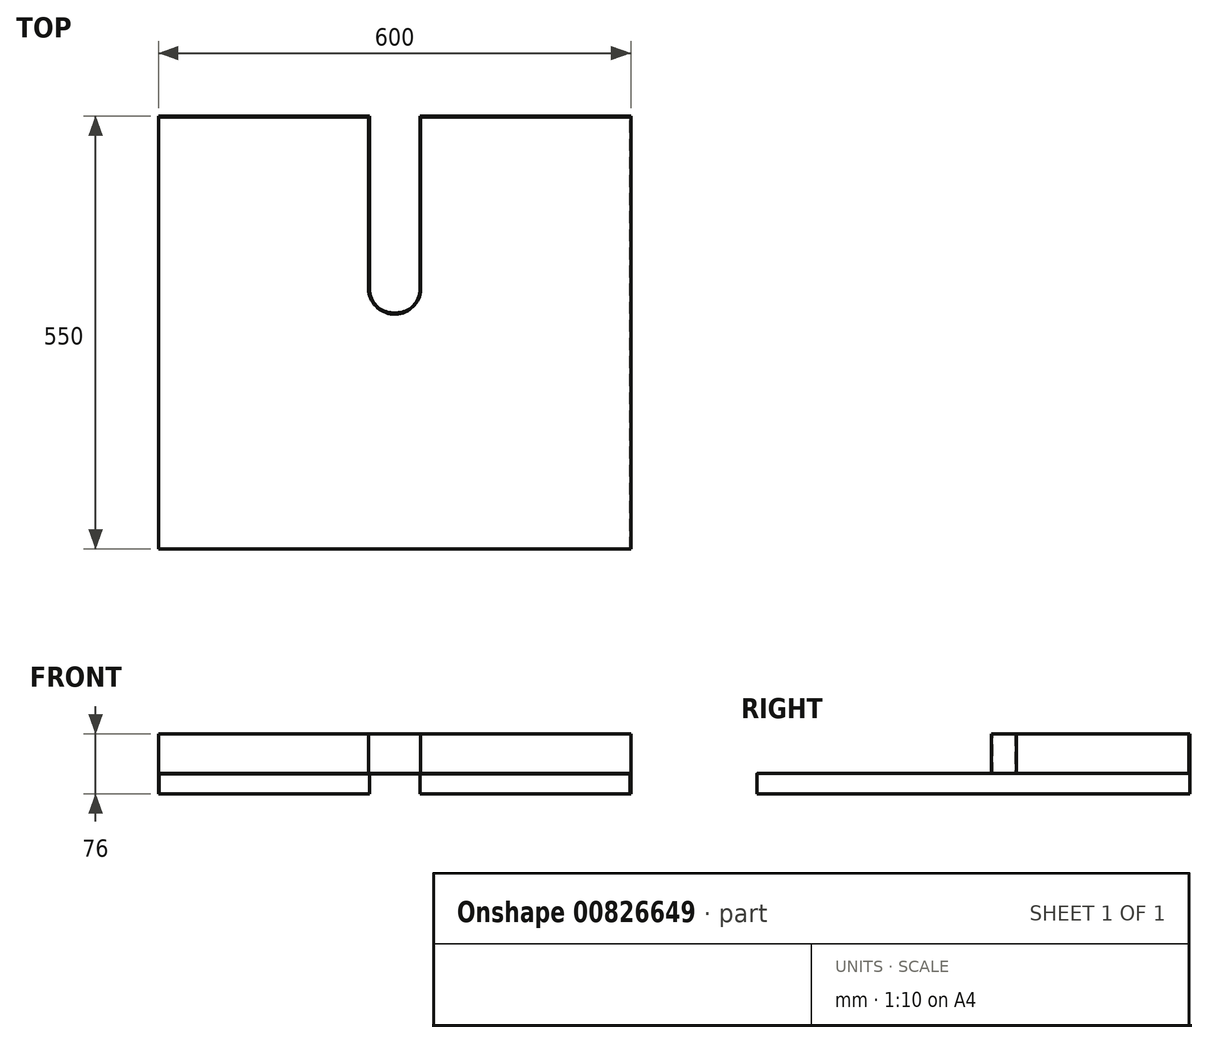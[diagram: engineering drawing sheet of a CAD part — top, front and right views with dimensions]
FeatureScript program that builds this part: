
annotation { "Feature Type Name" : "Feature", "Feature Type Description" : "" }
export const myFeature = defineFeature(function(context is Context, id is Id, definition is map)
    precondition{}
    {
        {
            var Q0;
            Q0=qCreatedBy(makeId("Top.planeOp"),FACE);
            var sketch = newSketch(context, id + "F0", { "sketchPlane" : qUnion([Q0])});
            skLineSegment(sketch, "E0.bottom", {"start": v(300, -275) * mm, "end": v(-300, -275) * mm});
            skLineSegment(sketch, "E0.top", {"start": v(300, 275) * mm, "end": v(-300, 275) * mm});
            skLineSegment(sketch, "E0.left", {"start": v(300, -275) * mm, "end": v(300, 275) * mm});
            skLineSegment(sketch, "E0.right", {"start": v(-300, -275) * mm, "end": v(-300, 275) * mm});
            skPoint(sketch, "E0.middle", {"position": v(0, 0) * mm});
            skSolve(sketch);
        }
        {
            var Q0;
            Q0=makeQuery(id+"F0.imprint","IMPRINT",FACE,{"disambiguationData":[TD([[makeQuery(id+"F0.imprint","IMPRINT",EDGE,{"derivedFrom":sQuery(id+"F0.wireOp",EDGE,"E0.bottom")}),-1.0]])]});
            extrude(context, id + "F1", {"entities" : qUnion([Q0]), "depth" : 1 * mm, "offsetDistance" : 25 * mm});
        }
        {
            var Q0;
            Q0=makeQuery(id+"F1.opExtrude","CAP_FACE",FACE,{"disambiguationData":[OSD([sQuery(id+"F0.wireOp",EDGE,"E0.bottom"),sQuery(id+"F0.wireOp",EDGE,"E0.top"),sQuery(id+"F0.wireOp",EDGE,"E0.left"),sQuery(id+"F0.wireOp",EDGE,"E0.right")])],"isStart":true});
            var sketch = newSketch(context, id + "F2", { "sketchPlane" : qUnion([Q0])});
            skLineSegment(sketch, "E1", {"start": v(299, 275) * mm, "end": v(299, -274) * mm});
            skLineSegment(sketch, "E2", {"start": v(-299, 275) * mm, "end": v(-299, -274) * mm});
            skLineSegment(sketch, "E3", {"start": v(-299, -274) * mm, "end": v(299, -274) * mm});
            skSolve(sketch);
        }
        {
            var Q0;
            {var subQ1=sQuery(id+"F2.wireOp",EDGE,"E1");Q0=makeQuery(id+"F2.imprint","IMPRINT",FACE,{"disambiguationData":[TD([[makeQuery(id+"F2.imprint","IMPRINT",EDGE,{"derivedFrom":subQ1}),1.0]])]});}
            extrude(context, id + "F3", {"entities" : qUnion([Q0]), "operationType" : NewBodyOperationType.ADD, "depth" : 25 * mm, "offsetDistance" : 25 * mm});
        }
        {
            var Q0;
            Q0=makeQuery(id+"F1.opExtrude","CAP_FACE",FACE,{"disambiguationData":[OSD([sQuery(id+"F0.wireOp",EDGE,"E0.bottom"),sQuery(id+"F0.wireOp",EDGE,"E0.top"),sQuery(id+"F0.wireOp",EDGE,"E0.left"),sQuery(id+"F0.wireOp",EDGE,"E0.right")])],"isStart":false});
            var sketch = newSketch(context, id + "F4", { "sketchPlane" : qUnion([Q0])});
            skLineSegment(sketch, "E4", {"start": v(0, 275) * mm, "end": v(0, -275) * mm, "construction": true});
            skLineSegment(sketch, "E5.bottom", {"start": v(32.08, 275) * mm, "end": v(-32.08, 275) * mm});
            skLineSegment(sketch, "E5.top", {"start": v(2.08, 25) * mm, "end": v(-2.08, 25) * mm});
            skLineSegment(sketch, "E5.left", {"start": v(32.08, 275) * mm, "end": v(32.08, 55) * mm});
            skLineSegment(sketch, "E5.right", {"start": v(-32.08, 275) * mm, "end": v(-32.08, 55) * mm});
            skPoint(sketch, "E5.middle", {"position": v(0, 150) * mm});
            skPoint(sketch, "E6.visualSharp", {"position": v(32.08, 25) * mm});
            skArc(sketch, "E6.filletArc", {"start": v(2.08, 25) * mm, "mid": v(23.3, 33.79) * mm, "end": v(32.08, 55) * mm});
            skPoint(sketch, "E7.visualSharp", {"position": v(-32.08, 25) * mm});
            skArc(sketch, "E7.filletArc", {"start": v(-32.08, 55) * mm, "mid": v(-23.3, 33.79) * mm, "end": v(-2.08, 25) * mm});
            skArc(sketch, "E8.0", {"start": v(-37.08, 55) * mm, "mid": v(-26.83, 30.25) * mm, "end": v(-2.08, 20) * mm});
            skLineSegment(sketch, "E8.1", {"start": v(-37.08, 275) * mm, "end": v(-37.08, 55) * mm});
            skLineSegment(sketch, "E9.MirrorCS", {"start": v(37.08, 275) * mm, "end": v(37.08, 55) * mm});
            skArc(sketch, "E10.MirrorCS", {"start": v(37.08, 55) * mm, "mid": v(26.83, 30.25) * mm, "end": v(2.08, 20) * mm});
            skSolve(sketch);
        }
        {
            var Q0;
            Q0=makeQuery(id+"F4.imprint","IMPRINT",FACE,{"disambiguationData":[TD([[makeQuery(id+"F4.imprint","IMPRINT",EDGE,{"derivedFrom":sQuery(id+"F4.wireOp",EDGE,"E5.bottom")}),1.0]])]});
            extrude(context, id + "F5", {"entities" : qUnion([Q0]), "operationType" : NewBodyOperationType.REMOVE, "endBound" : BoundingType.THROUGH_ALL, "oppositeDirection" : true, "depth" : 25 * mm, "offsetDistance" : 25 * mm});
        }
        {
            var Q0;
            Q0=makeQuery(id+"F1.opExtrude","CAP_FACE",FACE,{"disambiguationData":[OSD([sQuery(id+"F0.wireOp",EDGE,"E0.bottom"),sQuery(id+"F0.wireOp",EDGE,"E0.top"),sQuery(id+"F0.wireOp",EDGE,"E0.left"),sQuery(id+"F0.wireOp",EDGE,"E0.right")])],"isStart":false});
            var sketch = newSketch(context, id + "F6", { "sketchPlane" : qUnion([Q0])});
            skLineSegment(sketch, "E11", {"start": v(-33.08, 275) * mm, "end": v(-33.08, 52.7) * mm});
            skLineSegment(sketch, "E12", {"start": v(33.08, 275) * mm, "end": v(33.08, 55) * mm});
            skPoint(sketch, "E13.1.internal.snap0", {"position": v(0, 25) * mm});
            skArc(sketch, "E14", {"start": v(-33.08, 52.7) * mm, "mid": v(1.07, 23.3) * mm, "end": v(33.08, 55) * mm});
            skSolve(sketch);
        }
        {
            var Q0;
            Q0 = qSketchRegion(id + "F6", true);
            var Q1;
            {var subQ11=sQuery(id+"F6.wireOp",EDGE,"E11");Q1=makeQuery(id+"F6.imprint","IMPRINT",FACE,{"disambiguationData":[TD([[makeQuery(id+"F6.imprint","IMPRINT",EDGE,{"derivedFrom":subQ11}),1.0]])]});}
            extrude(context, id + "F7", {"entities" : qUnion([Q0, Q1]), "operationType" : NewBodyOperationType.ADD, "depth" : 50 * mm, "offsetDistance" : 25 * mm});
        }
        {
            var Q0;
            Q0=makeQuery(id+"F1.opExtrude","CAP_FACE",FACE,{"disambiguationData":[OSD([sQuery(id+"F0.wireOp",EDGE,"E0.bottom"),sQuery(id+"F0.wireOp",EDGE,"E0.top"),sQuery(id+"F0.wireOp",EDGE,"E0.left"),sQuery(id+"F0.wireOp",EDGE,"E0.right")])],"isStart":false});
            var sketch = newSketch(context, id + "F8", { "sketchPlane" : qUnion([Q0])});
            skLineSegment(sketch, "E15", {"start": v(-300, 274) * mm, "end": v(-33.08, 274) * mm});
            skLineSegment(sketch, "E16", {"start": v(33.08, 274) * mm, "end": v(300, 274) * mm});
            skSolve(sketch);
        }
        {
            var Q0;
            Q0 = qSketchRegion(id + "F8", true);
            var Q1;
            {var subQ0=sQuery(id+"F8.wireOp",EDGE,"E15");Q1=makeQuery(id+"F8.imprint","IMPRINT",FACE,{"disambiguationData":[TD([[makeQuery(id+"F8.imprint","IMPRINT",EDGE,{"derivedFrom":subQ0}),1.0]])]});}
            var Q2;
            {var subQ0=sQuery(id+"F8.wireOp",EDGE,"E16");Q2=makeQuery(id+"F8.imprint","IMPRINT",FACE,{"disambiguationData":[TD([[makeQuery(id+"F8.imprint","IMPRINT",EDGE,{"derivedFrom":subQ0}),1.0]])]});}
            extrude(context, id + "F9", {"entities" : qUnion([Q0, Q1, Q2]), "operationType" : NewBodyOperationType.ADD, "depth" : 50 * mm, "offsetDistance" : 25 * mm});
        }
        {
            var Q0;
            Q0=makeQuery(id+"F1.opExtrude","CAP_EDGE",EDGE,{"disambiguationData":[OSD([sQuery(id+"F0.wireOp",EDGE,"E0.right")])],"isStart":false});
            var Q1;
            Q1=makeQuery(id+"F1.opExtrude","CAP_EDGE",EDGE,{"disambiguationData":[OSD([sQuery(id+"F0.wireOp",EDGE,"E0.bottom")])],"isStart":false});
            var Q2;
            Q2=makeQuery(id+"F1.opExtrude","CAP_EDGE",EDGE,{"disambiguationData":[OSD([sQuery(id+"F0.wireOp",EDGE,"E0.left")])],"isStart":false});
            var Q3;
            Q3=makeQuery(id+"F9.opExtrude","CAP_EDGE",EDGE,{"disambiguationData":[OSD([sQuery(id+"F8.wireOp",EDGE,"E16")])],"isStart":true});
            var Q4;
            Q4=makeQuery(id+"F7.opExtrude","CAP_EDGE",EDGE,{"disambiguationData":[OSD([sQuery(id+"F6.wireOp",EDGE,"E12")])],"isStart":true});
            var Q5;
            Q5=makeQuery(id+"F7.opExtrude","CAP_EDGE",EDGE,{"disambiguationData":[OSD([sQuery(id+"F6.wireOp",EDGE,"E14")])],"isStart":true});
            var Q6;
            Q6=makeQuery(id+"F7.opExtrude","CAP_EDGE",EDGE,{"disambiguationData":[OSD([sQuery(id+"F6.wireOp",EDGE,"E11")])],"isStart":true});
            var Q7;
            Q7=makeQuery(id+"F9.opExtrude","CAP_EDGE",EDGE,{"disambiguationData":[OSD([sQuery(id+"F8.wireOp",EDGE,"E15")])],"isStart":true});
            fillet(context, id + "F10", {"entities" : qUnion([Q0, Q1, Q2, Q3, Q4, Q5, Q6, Q7]), "radius" : 1 * mm, "tangentPropagation" : true, "allowEdgeOverflow" : false});
        }
    });
